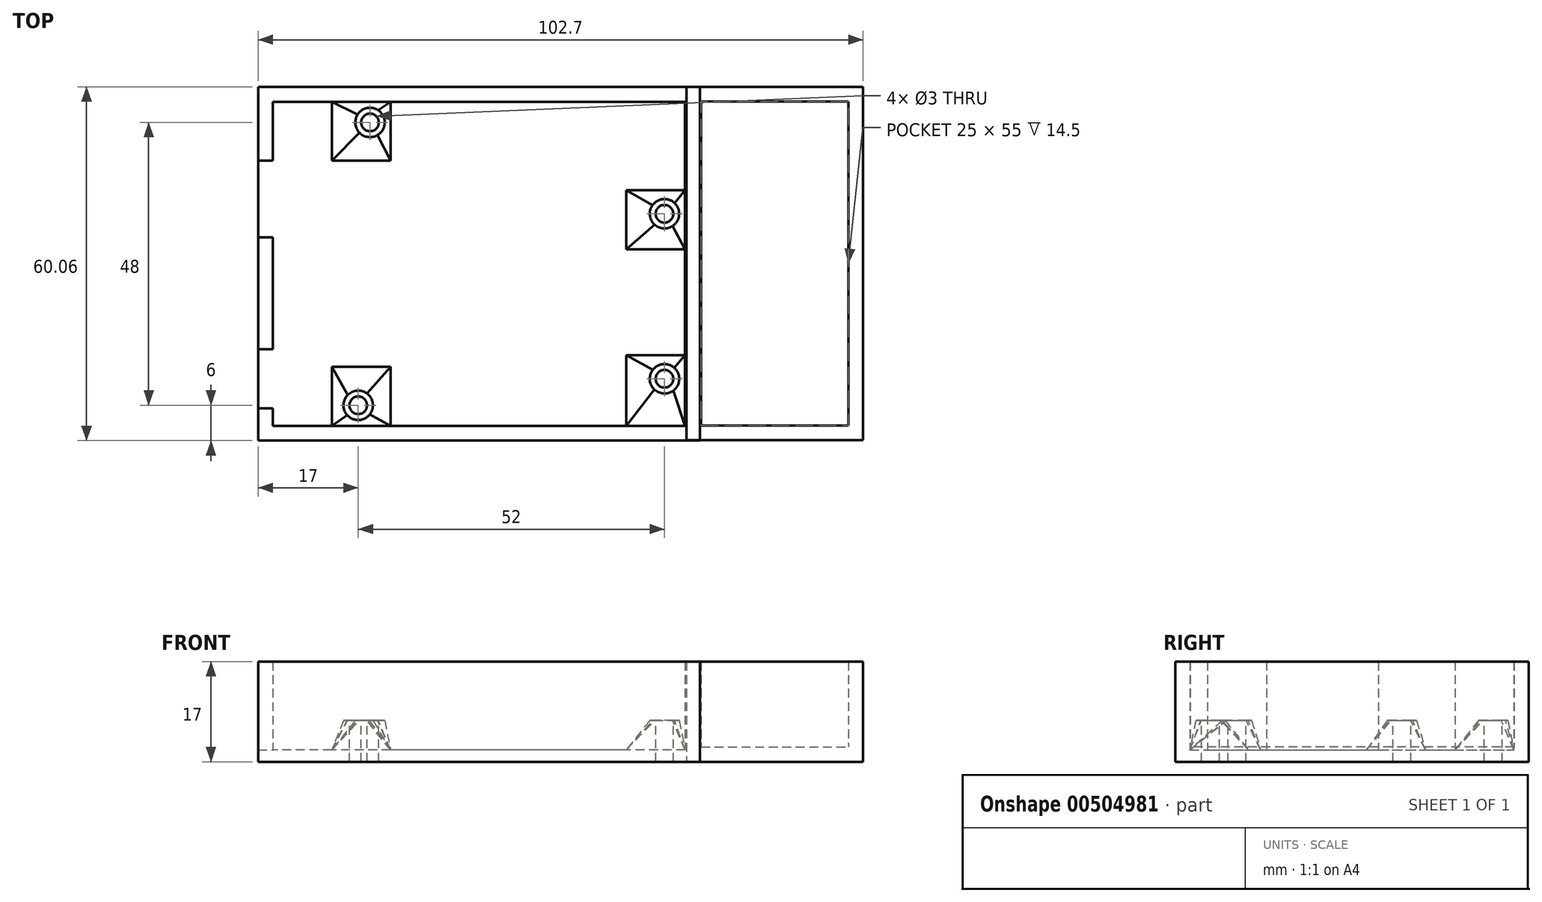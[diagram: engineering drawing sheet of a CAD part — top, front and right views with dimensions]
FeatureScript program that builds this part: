
annotation { "Feature Type Name" : "Feature", "Feature Type Description" : "" }
export const myFeature = defineFeature(function(context is Context, id is Id, definition is map)
    precondition{}
    {
        {
            var Q0;
            Q0=qCreatedBy(makeId("Top.planeOp"),FACE);
            var sketch = newSketch(context, id + "F0", { "sketchPlane" : qUnion([Q0])});
            skLineSegment(sketch, "E0.rect.bottom", {"start": v(37.5, -30) * mm, "end": v(-37.5, -30) * mm});
            skLineSegment(sketch, "E0.rect.top", {"start": v(37.5, 30) * mm, "end": v(-37.5, 30) * mm});
            skLineSegment(sketch, "E0.rect.left", {"start": v(37.5, -30) * mm, "end": v(37.5, 30) * mm});
            skLineSegment(sketch, "E0.rect.right", {"start": v(-37.5, -30) * mm, "end": v(-37.5, 30) * mm});
            skPoint(sketch, "E0.rect.middle", {"position": v(0, 0) * mm});
            skSolve(sketch);
        }
        {
            var Q0;
            Q0=qSketchRegion(id+"F0",true);
            extrude(context, id + "F1", {"entities" : qUnion([Q0]), "depth" : 2 * mm});
        }
        {
            var Q0;
            Q0=makeQuery(id+"F1.opExtrude","CAP_FACE",FACE,{"disambiguationData":[OSD([sQuery(id+"F0.wireOp",EDGE,"E0.rect.bottom"),sQuery(id+"F0.wireOp",EDGE,"E0.rect.top"),sQuery(id+"F0.wireOp",EDGE,"E0.rect.left"),sQuery(id+"F0.wireOp",EDGE,"E0.rect.right")])],"isStart":false});
            var sketch = newSketch(context, id + "F2", { "sketchPlane" : qUnion([Q0])});
            skLineSegment(sketch, "E1.rect.bottom", {"start": v(35, -27.5) * mm, "end": v(-35, -27.5) * mm});
            skLineSegment(sketch, "E1.rect.top", {"start": v(35, 27.5) * mm, "end": v(-35, 27.5) * mm});
            skLineSegment(sketch, "E1.rect.left", {"start": v(35, -27.5) * mm, "end": v(35, 27.5) * mm});
            skLineSegment(sketch, "E1.rect.right", {"start": v(-35, -27.5) * mm, "end": v(-35, 27.5) * mm});
            skPoint(sketch, "E1.rect.middle", {"position": v(0, 0) * mm});
            skLineSegment(sketch, "E2.rect.bottom", {"start": v(37.5, -30) * mm, "end": v(-37.5, -30) * mm});
            skLineSegment(sketch, "E2.rect.top", {"start": v(37.5, 30) * mm, "end": v(-37.5, 30) * mm});
            skLineSegment(sketch, "E2.rect.left", {"start": v(37.5, -30) * mm, "end": v(37.5, 30) * mm});
            skLineSegment(sketch, "E2.rect.right", {"start": v(-37.5, -30) * mm, "end": v(-37.5, 30) * mm});
            skSolve(sketch);
        }
        {
            var Q0;
            Q0=qSketchRegion(id+"F2",true);
            extrude(context, id + "F3", {"entities" : qUnion([Q0]), "operationType" : NewBodyOperationType.ADD, "depth" : 15 * mm});
        }
        {
            var Q0;
            Q0=makeQuery(id+"F1.opExtrude","CAP_FACE",FACE,{"disambiguationData":[OSD([sQuery(id+"F0.wireOp",EDGE,"E0.rect.bottom"),sQuery(id+"F0.wireOp",EDGE,"E0.rect.top"),sQuery(id+"F0.wireOp",EDGE,"E0.rect.left"),sQuery(id+"F0.wireOp",EDGE,"E0.rect.right")])],"isStart":false});
            var sketch = newSketch(context, id + "F4", { "sketchPlane" : qUnion([Q0])});
            skLineSegment(sketch, "E3.bottom", {"start": v(-25, 27.5) * mm, "end": v(-15, 27.5) * mm});
            skLineSegment(sketch, "E3.top", {"start": v(-25, 17.5) * mm, "end": v(-15, 17.5) * mm});
            skLineSegment(sketch, "E3.left", {"start": v(-25, 27.5) * mm, "end": v(-25, 17.5) * mm});
            skLineSegment(sketch, "E3.right", {"start": v(-15, 27.5) * mm, "end": v(-15, 17.5) * mm});
            skLineSegment(sketch, "E4.bottom", {"start": v(-25, -27.5) * mm, "end": v(-15, -27.5) * mm});
            skLineSegment(sketch, "E4.top", {"start": v(-25, -17.5) * mm, "end": v(-15, -17.5) * mm});
            skLineSegment(sketch, "E4.left", {"start": v(-25, -27.5) * mm, "end": v(-25, -17.5) * mm});
            skLineSegment(sketch, "E4.right", {"start": v(-15, -27.5) * mm, "end": v(-15, -17.5) * mm});
            skLineSegment(sketch, "E5.bottom", {"start": v(35, -27.5) * mm, "end": v(25, -27.5) * mm});
            skLineSegment(sketch, "E5.top", {"start": v(35, -15.5) * mm, "end": v(25, -15.5) * mm});
            skLineSegment(sketch, "E5.left", {"start": v(35, -27.5) * mm, "end": v(35, -15.5) * mm});
            skLineSegment(sketch, "E5.right", {"start": v(25, -27.5) * mm, "end": v(25, -15.5) * mm});
            skLineSegment(sketch, "E6.bottom", {"start": v(35, 12.5) * mm, "end": v(25, 12.5) * mm});
            skLineSegment(sketch, "E6.top", {"start": v(35, 2.5) * mm, "end": v(25, 2.5) * mm});
            skLineSegment(sketch, "E6.left", {"start": v(35, 12.5) * mm, "end": v(35, 2.5) * mm});
            skLineSegment(sketch, "E6.right", {"start": v(25, 12.5) * mm, "end": v(25, 2.5) * mm});
            skSolve(sketch);
        }
        {
            var Q0;
            Q0=makeQuery(id+"F4.imprint","IMPRINT",FACE,{"disambiguationData":[TD([[makeQuery(id+"F4.imprint","IMPRINT",EDGE,{"derivedFrom":sQuery(id+"F4.wireOp",EDGE,"E3.top")}),-1.0]])]});
            cPlane(context, id + "F5", {"entities" : qUnion([Q0]), "cplaneType" : CPlaneType.OFFSET, "offset" : 5 * mm, "width" : 150 * mm, "height" : 150 * mm});
        }
        {
            var Q0;
            Q0=qCreatedBy(id+"F5.planeOp",FACE);
            var sketch = newSketch(context, id + "F6", { "sketchPlane" : qUnion([Q0])});
            skArc(sketch, "E7", {"start": v(-17.2, 21.86) * mm, "mid": v(-16, 23.94) * mm, "end": v(-17.1, 26.07) * mm});
            skArc(sketch, "E8", {"start": v(-17.1, 26.07) * mm, "mid": v(-19, 26.45) * mm, "end": v(-20.6, 25.36) * mm});
            skArc(sketch, "E9", {"start": v(-20.6, 25.36) * mm, "mid": v(-20.99, 23.76) * mm, "end": v(-20.3, 22.26) * mm});
            skArc(sketch, "E10", {"start": v(-20.3, 22.26) * mm, "mid": v(-18.82, 21.52) * mm, "end": v(-17.2, 21.86) * mm});
            skArc(sketch, "E11", {"start": v(-22.3, -22.26) * mm, "mid": v(-23, -23.92) * mm, "end": v(-22.4, -25.63) * mm});
            skArc(sketch, "E12", {"start": v(-19.03, -21.98) * mm, "mid": v(-20.71, -21.5) * mm, "end": v(-22.3, -22.26) * mm});
            skArc(sketch, "E13", {"start": v(-18.54, -25.56) * mm, "mid": v(-18.02, -23.66) * mm, "end": v(-19.03, -21.98) * mm});
            skArc(sketch, "E14", {"start": v(-22.4, -25.63) * mm, "mid": v(-20.45, -26.5) * mm, "end": v(-18.54, -25.56) * mm});
            skArc(sketch, "E15", {"start": v(29.8, -21.33) * mm, "mid": v(31.36, -22) * mm, "end": v(32.98, -21.51) * mm});
            skArc(sketch, "E16", {"start": v(29.53, -17.96) * mm, "mid": v(29, -19.7) * mm, "end": v(29.8, -21.33) * mm});
            skArc(sketch, "E17", {"start": v(33.16, -17.63) * mm, "mid": v(31.27, -17.01) * mm, "end": v(29.53, -17.96) * mm});
            skArc(sketch, "E18", {"start": v(32.98, -21.51) * mm, "mid": v(34, -19.61) * mm, "end": v(33.16, -17.63) * mm});
            skArc(sketch, "E19", {"start": v(32.9, 6.43) * mm, "mid": v(34, 8.3) * mm, "end": v(33.23, 10.3) * mm});
            skArc(sketch, "E20", {"start": v(33.23, 10.3) * mm, "mid": v(31.28, 11) * mm, "end": v(29.48, 9.98) * mm});
            skArc(sketch, "E21", {"start": v(29.48, 9.98) * mm, "mid": v(29.01, 8.25) * mm, "end": v(29.82, 6.65) * mm});
            skArc(sketch, "E22", {"start": v(29.82, 6.65) * mm, "mid": v(31.32, 6) * mm, "end": v(32.9, 6.43) * mm});
            skSolve(sketch);
        }
        {
            var Q1;
            Q1=makeQuery(id+"F4.imprint","IMPRINT",FACE,{"disambiguationData":[TD([[makeQuery(id+"F4.imprint","IMPRINT",EDGE,{"derivedFrom":sQuery(id+"F4.wireOp",EDGE,"E3.bottom")}),1.0]])]});
            var Q2;
            Q2=makeQuery(id+"F6.imprint","IMPRINT",FACE,{"disambiguationData":[TD([[makeQuery(id+"F6.imprint","IMPRINT",EDGE,{"derivedFrom":sQuery(id+"F6.wireOp",EDGE,"E7")}),1.0]])]});
            loft(context, id + "F7", {"operationType" : NewBodyOperationType.ADD, "sheetProfilesArray" : [{ "sheetProfileEntities" : qUnion([Q1]) }, { "sheetProfileEntities" : qUnion([Q2]) }]});
        }
        {
            var Q1;
            Q1=makeQuery(id+"F4.imprint","IMPRINT",FACE,{"disambiguationData":[TD([[makeQuery(id+"F4.imprint","IMPRINT",EDGE,{"derivedFrom":sQuery(id+"F4.wireOp",EDGE,"E6.bottom")}),1.0]])]});
            var Q2;
            Q2=makeQuery(id+"F6.imprint","IMPRINT",FACE,{"disambiguationData":[TD([[makeQuery(id+"F6.imprint","IMPRINT",EDGE,{"derivedFrom":sQuery(id+"F6.wireOp",EDGE,"E19")}),1.0]])]});
            loft(context, id + "F8", {"operationType" : NewBodyOperationType.ADD, "sheetProfilesArray" : [{ "sheetProfileEntities" : qUnion([Q1]) }, { "sheetProfileEntities" : qUnion([Q2]) }]});
        }
        {
            var Q1;
            Q1=makeQuery(id+"F4.imprint","IMPRINT",FACE,{"disambiguationData":[TD([[makeQuery(id+"F4.imprint","IMPRINT",EDGE,{"derivedFrom":sQuery(id+"F4.wireOp",EDGE,"E5.bottom")}),-1.0]])]});
            var Q2;
            Q2=makeQuery(id+"F6.imprint","IMPRINT",FACE,{"disambiguationData":[TD([[makeQuery(id+"F6.imprint","IMPRINT",EDGE,{"derivedFrom":sQuery(id+"F6.wireOp",EDGE,"E15")}),1.0]])]});
            loft(context, id + "F9", {"operationType" : NewBodyOperationType.ADD, "sheetProfilesArray" : [{ "sheetProfileEntities" : qUnion([Q1]) }, { "sheetProfileEntities" : qUnion([Q2]) }]});
        }
        {
            var Q1;
            Q1=makeQuery(id+"F4.imprint","IMPRINT",FACE,{"disambiguationData":[TD([[makeQuery(id+"F4.imprint","IMPRINT",EDGE,{"derivedFrom":sQuery(id+"F4.wireOp",EDGE,"E4.bottom")}),-1.0]])]});
            var Q2;
            Q2=makeQuery(id+"F6.imprint","IMPRINT",FACE,{"disambiguationData":[TD([[makeQuery(id+"F6.imprint","IMPRINT",EDGE,{"derivedFrom":sQuery(id+"F6.wireOp",EDGE,"E11")}),1.0]])]});
            loft(context, id + "F10", {"operationType" : NewBodyOperationType.ADD, "sheetProfilesArray" : [{ "sheetProfileEntities" : qUnion([Q1]) }, { "sheetProfileEntities" : qUnion([Q2]) }]});
        }
        {
            var Q0;
            Q0=sQuery(id+"F6.wireOp",VERTEX,"E8.center");
            var Q1;
            Q1=sQuery(id+"F6.wireOp",VERTEX,"E19.center");
            var Q2;
            Q2=sQuery(id+"F6.wireOp",VERTEX,"E17.center");
            var Q3;
            Q3=sQuery(id+"F6.wireOp",VERTEX,"E12.center");
            var Q4;
            Q4=makeQuery(id+"F1.opExtrude","SWEPT_BODY",BODY,{"disambiguationData":[OSD([sQuery(id+"F0.wireOp",EDGE,"E0.rect.bottom"),sQuery(id+"F0.wireOp",EDGE,"E0.rect.top"),sQuery(id+"F0.wireOp",EDGE,"E0.rect.left"),sQuery(id+"F0.wireOp",EDGE,"E0.rect.right")])]});
            hole(context, id + "F11", {"style" : HoleStyle.SIMPLE, "holeDiameter" : 3 * mm, "endStyle" : HoleEndStyle.THROUGH, "locations" : qUnion([Q0, Q1, Q2, Q3]), "scope" : qUnion([Q4])});
        }
        {
            var Q0;
            Q0=makeQuery(id+"F3.opExtrude","SWEPT_FACE",FACE,{"disambiguationData":[OSD([sQuery(id+"F2.wireOp",EDGE,"E1.rect.right")])]});
            var sketch = newSketch(context, id + "F12", { "sketchPlane" : qUnion([Q0])});
            skLineSegment(sketch, "E23.bottom", {"start": v(-24.5, 17) * mm, "end": v(-14.5, 17) * mm});
            skLineSegment(sketch, "E23.top", {"start": v(-24.5, 2) * mm, "end": v(-14.5, 2) * mm});
            skLineSegment(sketch, "E23.left", {"start": v(-24.5, 17) * mm, "end": v(-24.5, 2) * mm});
            skLineSegment(sketch, "E23.right", {"start": v(-14.5, 17) * mm, "end": v(-14.5, 2) * mm});
            skLineSegment(sketch, "E24.bottom", {"start": v(4.5, 17) * mm, "end": v(17.5, 17) * mm});
            skLineSegment(sketch, "E24.top", {"start": v(4.5, 2) * mm, "end": v(17.5, 2) * mm});
            skLineSegment(sketch, "E24.left", {"start": v(4.5, 17) * mm, "end": v(4.5, 2) * mm});
            skLineSegment(sketch, "E24.right", {"start": v(17.5, 17) * mm, "end": v(17.5, 2) * mm});
            skSolve(sketch);
        }
        {
            var Q0;
            Q0=qSketchRegion(id+"F12",true);
            extrude(context, id + "F13", {"entities" : qUnion([Q0]), "operationType" : NewBodyOperationType.REMOVE, "endBound" : BoundingType.UP_TO_NEXT, "oppositeDirection" : true, "depth" : 25 * mm});
        }
        {
            var Q0;
            Q0=qCreatedBy(makeId("Top.planeOp"),FACE);
            var sketch = newSketch(context, id + "F14", { "sketchPlane" : qUnion([Q0])});
            skLineSegment(sketch, "E25.bottom", {"start": v(35.2, 30.06) * mm, "end": v(65.2, 30.06) * mm});
            skLineSegment(sketch, "E25.top", {"start": v(35.2, -29.94) * mm, "end": v(65.2, -29.94) * mm});
            skLineSegment(sketch, "E25.left", {"start": v(35.2, 30.06) * mm, "end": v(35.2, -29.94) * mm});
            skLineSegment(sketch, "E25.right", {"start": v(65.2, 30.06) * mm, "end": v(65.2, -29.94) * mm});
            skSolve(sketch);
        }
        {
            var Q0;
            Q0=makeQuery(id+"F14.imprint","IMPRINT",FACE,{"disambiguationData":[TD([[makeQuery(id+"F14.imprint","IMPRINT",EDGE,{"derivedFrom":sQuery(id+"F14.wireOp",EDGE,"E25.bottom")}),-1.0]])]});
            extrude(context, id + "F15", {"entities" : qUnion([Q0]), "depth" : 17 * mm});
        }
        {
            var Q0;
            Q0=makeQuery(id+"F15.opExtrude","CAP_FACE",FACE,{"disambiguationData":[OSD([sQuery(id+"F14.wireOp",EDGE,"E25.bottom"),sQuery(id+"F14.wireOp",EDGE,"E25.top"),sQuery(id+"F14.wireOp",EDGE,"E25.left"),sQuery(id+"F14.wireOp",EDGE,"E25.right")])],"isStart":false});
            shell(context, id + "F16", {"entities" : qUnion([Q0]), "thickness" : 2.5 * mm});
        }
    });
